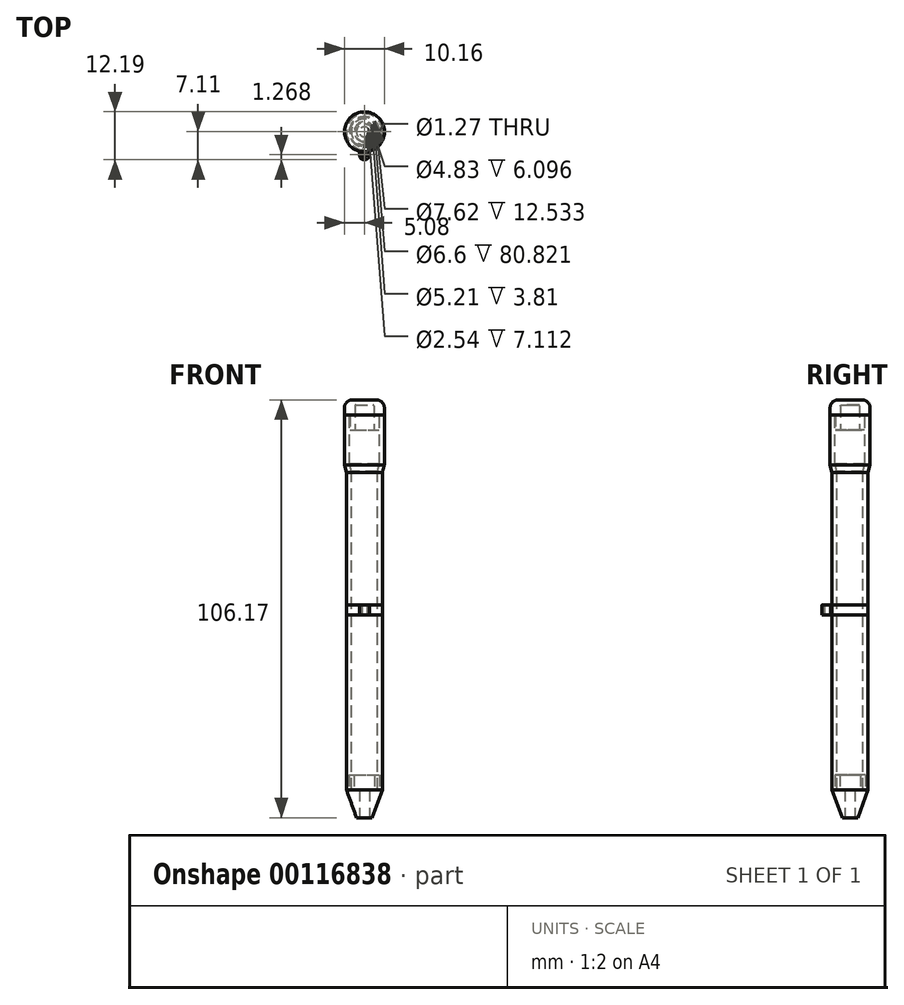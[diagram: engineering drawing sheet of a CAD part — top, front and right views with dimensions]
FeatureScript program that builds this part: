
annotation { "Feature Type Name" : "Feature", "Feature Type Description" : "" }
export const myFeature = defineFeature(function(context is Context, id is Id, definition is map)
    precondition{}
    {
        {
            var Q0;
            Q0=qCreatedBy(makeId("Front.planeOp"),FACE);
            var sketch = newSketch(context, id + "F0", { "sketchPlane" : qUnion([Q0])});
            skLineSegment(sketch, "E0", {"start": v(0, 50.8) * mm, "end": v(0, -44.45) * mm, "construction": true});
            skLineSegment(sketch, "E1", {"start": v(0, 50.8) * mm, "end": v(5.08, 50.8) * mm, "construction": true});
            skLineSegment(sketch, "E2", {"start": v(5.08, 50.8) * mm, "end": v(5.08, 38.1) * mm});
            skLineSegment(sketch, "E3", {"start": v(5.08, 38.1) * mm, "end": v(4.57, 36.2) * mm});
            skLineSegment(sketch, "E4", {"start": v(4.57, 36.2) * mm, "end": v(4.57, -44.45) * mm});
            skLineSegment(sketch, "E5", {"start": v(4.57, -44.45) * mm, "end": v(0, -44.45) * mm, "construction": true});
            skLineSegment(sketch, "E6.0", {"start": v(3.3, 36.37) * mm, "end": v(3.3, -44.45) * mm});
            skLineSegment(sketch, "E6.1", {"start": v(3.8, 38.27) * mm, "end": v(3.3, 36.37) * mm});
            skLineSegment(sketch, "E6.2", {"start": v(3.8, 50.8) * mm, "end": v(3.81, 38.27) * mm});
            skLineSegment(sketch, "E7", {"start": v(3.8, 50.8) * mm, "end": v(5.08, 50.8) * mm});
            skLineSegment(sketch, "E8", {"start": v(3.3, -44.45) * mm, "end": v(4.57, -44.45) * mm});
            skSolve(sketch);
        }
        {
            var Q0;
            Q0=makeQuery(id+"F0.imprint","IMPRINT",FACE,{"disambiguationData":[TD([[makeQuery(id+"F0.imprint","IMPRINT",EDGE,{"derivedFrom":sQuery(id+"F0.wireOp",EDGE,"E2")}),-1.0]])]});
            var Q1;
            Q1=sQuery(id+"F0.wireOp",EDGE,"E0");
            revolve(context, id + "F1", {"entities" : qUnion([Q0]), "axis" : qUnion([Q1]), "revolveType" : RevolveType.FULL});
        }
        {
            var Q0;
            Q0=qCreatedBy(makeId("Front.planeOp"),FACE);
            var sketch = newSketch(context, id + "F2", { "sketchPlane" : qUnion([Q0])});
            skLineSegment(sketch, "E9", {"start": v(0, 54.61) * mm, "end": v(5.08, 54.61) * mm});
            skLineSegment(sketch, "E10", {"start": v(5.08, 54.61) * mm, "end": v(5.08, 50.8) * mm});
            skLineSegment(sketch, "E11", {"start": v(5.08, 50.8) * mm, "end": v(5.08, 27.3) * mm, "construction": true});
            skLineSegment(sketch, "E12", {"start": v(0, 0) * mm, "end": v(0, 53.75) * mm, "construction": true});
            skLineSegment(sketch, "E13", {"start": v(5.08, 50.8) * mm, "end": v(3.68, 50.8) * mm});
            skLineSegment(sketch, "E14", {"start": v(3.68, 50.8) * mm, "end": v(3.68, 47) * mm});
            skLineSegment(sketch, "E15.0", {"start": v(2.41, 53.34) * mm, "end": v(2.41, 47) * mm});
            skLineSegment(sketch, "E15.3", {"start": v(0, 53.34) * mm, "end": v(2.41, 53.34) * mm});
            skLineSegment(sketch, "E16", {"start": v(0, 54.61) * mm, "end": v(0, 53.34) * mm});
            skLineSegment(sketch, "E17", {"start": v(2.41, 47) * mm, "end": v(3.68, 47) * mm});
            skSolve(sketch);
        }
        {
            var Q0;
            Q0=makeQuery(id+"F2.imprint","IMPRINT",FACE,{"disambiguationData":[TD([[makeQuery(id+"F2.imprint","IMPRINT",EDGE,{"derivedFrom":sQuery(id+"F2.wireOp",EDGE,"E9")}),-1.0]])]});
            var Q1;
            Q1=sQuery(id+"F2.wireOp",EDGE,"E12");
            revolve(context, id + "F3", {"entities" : qUnion([Q0]), "axis" : qUnion([Q1]), "revolveType" : RevolveType.FULL});
        }
        {
            var Q0;
            Q0=makeQuery(id+"F3.opRevolve","SWEPT_EDGE",EDGE,{"disambiguationData":[OSD([sQuery(id+"F2.wireOp",EDGE,"E9"),sQuery(id+"F2.wireOp",EDGE,"E10")])]});
            fillet(context, id + "F4", {"entities" : qUnion([Q0]), "radius" : 2.03 * mm, "tangentPropagation" : true, "allowEdgeOverflow" : false});
        }
        {
            var Q0;
            Q0=makeQuery(id+"F3.opRevolve","SWEPT_EDGE",EDGE,{"disambiguationData":[OSD([sQuery(id+"F2.wireOp",EDGE,"E15.0"),sQuery(id+"F2.wireOp",EDGE,"E15.3")])]});
            fillet(context, id + "F5", {"entities" : qUnion([Q0]), "radius" : 0.25 * mm, "tangentPropagation" : true, "allowEdgeOverflow" : false});
        }
        {
            var Q0;
            Q0=qCreatedBy(makeId("Front.planeOp"),FACE);
            var sketch = newSketch(context, id + "F6", { "sketchPlane" : qUnion([Q0])});
            skLineSegment(sketch, "E18", {"start": v(0, -71.53) * mm, "end": v(0, -44.45) * mm, "construction": true});
            skLineSegment(sketch, "E19.0", {"start": v(-4.57, -44.45) * mm, "end": v(4.57, -44.45) * mm, "construction": true});
            skLineSegment(sketch, "E20", {"start": v(4.57, -1.9) * mm, "end": v(4.57, -63.5) * mm, "construction": true});
            skLineSegment(sketch, "E21", {"start": v(3.87, -40.64) * mm, "end": v(3.87, -44.45) * mm});
            skLineSegment(sketch, "E22", {"start": v(3.87, -44.45) * mm, "end": v(4.57, -44.45) * mm});
            skLineSegment(sketch, "E23", {"start": v(4.57, -44.45) * mm, "end": v(1.98, -51.56) * mm});
            skLineSegment(sketch, "E24", {"start": v(1.98, -51.56) * mm, "end": v(1.27, -51.56) * mm});
            skLineSegment(sketch, "E25", {"start": v(1.27, -51.56) * mm, "end": v(1.27, -44.45) * mm});
            skLineSegment(sketch, "E26", {"start": v(2.6, -40.64) * mm, "end": v(3.87, -40.64) * mm});
            skLineSegment(sketch, "E27", {"start": v(1.27, -44.45) * mm, "end": v(2.6, -44.45) * mm});
            skLineSegment(sketch, "E28", {"start": v(2.6, -44.45) * mm, "end": v(2.6, -40.64) * mm});
            skPoint(sketch, "E29.orphan", {"position": v(1.27, -40.64) * mm});
            skSolve(sketch);
        }
        {
            var Q0;
            Q0=makeQuery(id+"F6.imprint","IMPRINT",FACE,{"disambiguationData":[TD([[makeQuery(id+"F6.imprint","IMPRINT",EDGE,{"derivedFrom":sQuery(id+"F6.wireOp",EDGE,"E21")}),-1.0]])]});
            var Q1;
            Q1=sQuery(id+"F6.wireOp",EDGE,"E18");
            revolve(context, id + "F7", {"entities" : qUnion([Q0]), "axis" : qUnion([Q1]), "revolveType" : RevolveType.FULL});
        }
        {
            var Q0;
            Q0=qCreatedBy(makeId("Top.planeOp"),FACE);
            var sketch = newSketch(context, id + "F8", { "sketchPlane" : qUnion([Q0])});
            skCircle(sketch, "E30.0", {"center": v(0, 0) * mm, "radius": 4.57 * mm});
            skCircle(sketch, "E31", {"center": v(0, 0) * mm, "radius": 5.08 * mm});
            skSolve(sketch);
        }
        {
            var Q0;
            Q0=makeQuery(id+"F8.imprint","IMPRINT",FACE,{"disambiguationData":[TD([[makeQuery(id+"F8.imprint","IMPRINT",EDGE,{"derivedFrom":sQuery(id+"F8.wireOp",EDGE,"E30.0")}),1.0]])]});
            extrude(context, id + "F9", {"entities" : qUnion([Q0]), "depth" : 2.54 * mm});
        }
        {
            var Q0;
            Q0=qCreatedBy(makeId("Top.planeOp"),FACE);
            var sketch = newSketch(context, id + "F10", { "sketchPlane" : qUnion([Q0])});
            skCircle(sketch, "E32", {"center": v(0, -5.84) * mm, "radius": 0.64 * mm});
            skArc(sketch, "E33", {"start": v(-1.27, -5.84) * mm, "mid": v(0, -7.11) * mm, "end": v(1.27, -5.84) * mm});
            skLineSegment(sketch, "E34", {"start": v(1.27, -5.84) * mm, "end": v(1.27, -4.92) * mm});
            skArc(sketch, "E35.0", {"start": v(-1.27, -4.92) * mm, "mid": v(0, -5.08) * mm, "end": v(1.27, -4.92) * mm});
            skLineSegment(sketch, "E36", {"start": v(-1.27, -5.84) * mm, "end": v(-1.27, -4.92) * mm});
            skSolve(sketch);
        }
        {
            var Q0;
            Q0=makeQuery(id+"F10.imprint","IMPRINT",FACE,{"disambiguationData":[TD([[makeQuery(id+"F10.imprint","IMPRINT",EDGE,{"derivedFrom":sQuery(id+"F10.wireOp",EDGE,"E32")}),-1.0]])]});
            var Q1;
            Q1=makeQuery(id+"F9.opExtrude","CAP_FACE",FACE,{"disambiguationData":[OSD([sQuery(id+"F8.wireOp",EDGE,"E30.0"),sQuery(id+"F8.wireOp",EDGE,"E31")])],"isStart":false});
            extrude(context, id + "F11", {"entities" : qUnion([Q0]), "operationType" : NewBodyOperationType.ADD, "endBound" : BoundingType.UP_TO_SURFACE, "endBoundEntityFace" : qUnion([Q1]), "depth" : 25.4 * mm});
        }
    });
